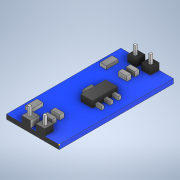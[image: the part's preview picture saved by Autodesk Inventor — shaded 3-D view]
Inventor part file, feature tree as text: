
AUTODESK INVENTOR PART (.ipt)
format: ipt  version: 2021 (Build 250183000, 183)  size: 262,656 bytes
history: native  units: mm
features: sketch x7, extrude x6
ambient origin geometry x8: Origin, YZ Plane, XZ Plane, XY Plane, X Axis, Y Axis, Z Axis, Center Point
bodies: Solid1 (feature_tree)
feature tree (13):
  extrude  "Extrusion1"  Depth=26.0mm
  extrude  "Extrusion2"  Depth=2.0mm
  extrude  "Extrusion3"  Depth=2.0mm
  extrude  "Extrusion4"  Depth=2.0mm
  extrude  "Extrusion5"  Depth=0.5mm
  sketch  "Sketch6"  dims[d12=0.5mm d13=0.5mm]
  extrude  "Extrusion6"  Depth=0.5mm
  sketch  "Sketch1"  dims[d0=12.0mm d1=26.0mm]
  sketch  "Sketch2"  dims[d2=1.0mm d3=0.0mm d4=2.0mm]
  sketch  "Sketch3"  dims[d5=2.0mm d6=2.0mm]
  sketch  "Sketch4"  dims[d7=2.0mm d8=2.0mm]
  sketch  "Sketch5"  dims[d9=1.5mm d10=0.0mm d11=0.5mm]
  sketch  "Sketch7"  dims[d14=0.5mm d15=0.5mm d16=0.5mm d17=2.0mm d18=0.0mm d19=2.0mm d20=1.0mm d21=2.0mm d22=1.0mm d23=2.0mm d24=1.0mm d25=2.0mm d26=1.0mm d27=1.0mm d28=0.0mm d29=0.7mm d30=0.0mm d31=0.7mm d32=0.0mm d33=0.5mm d34=0.872665mm]
